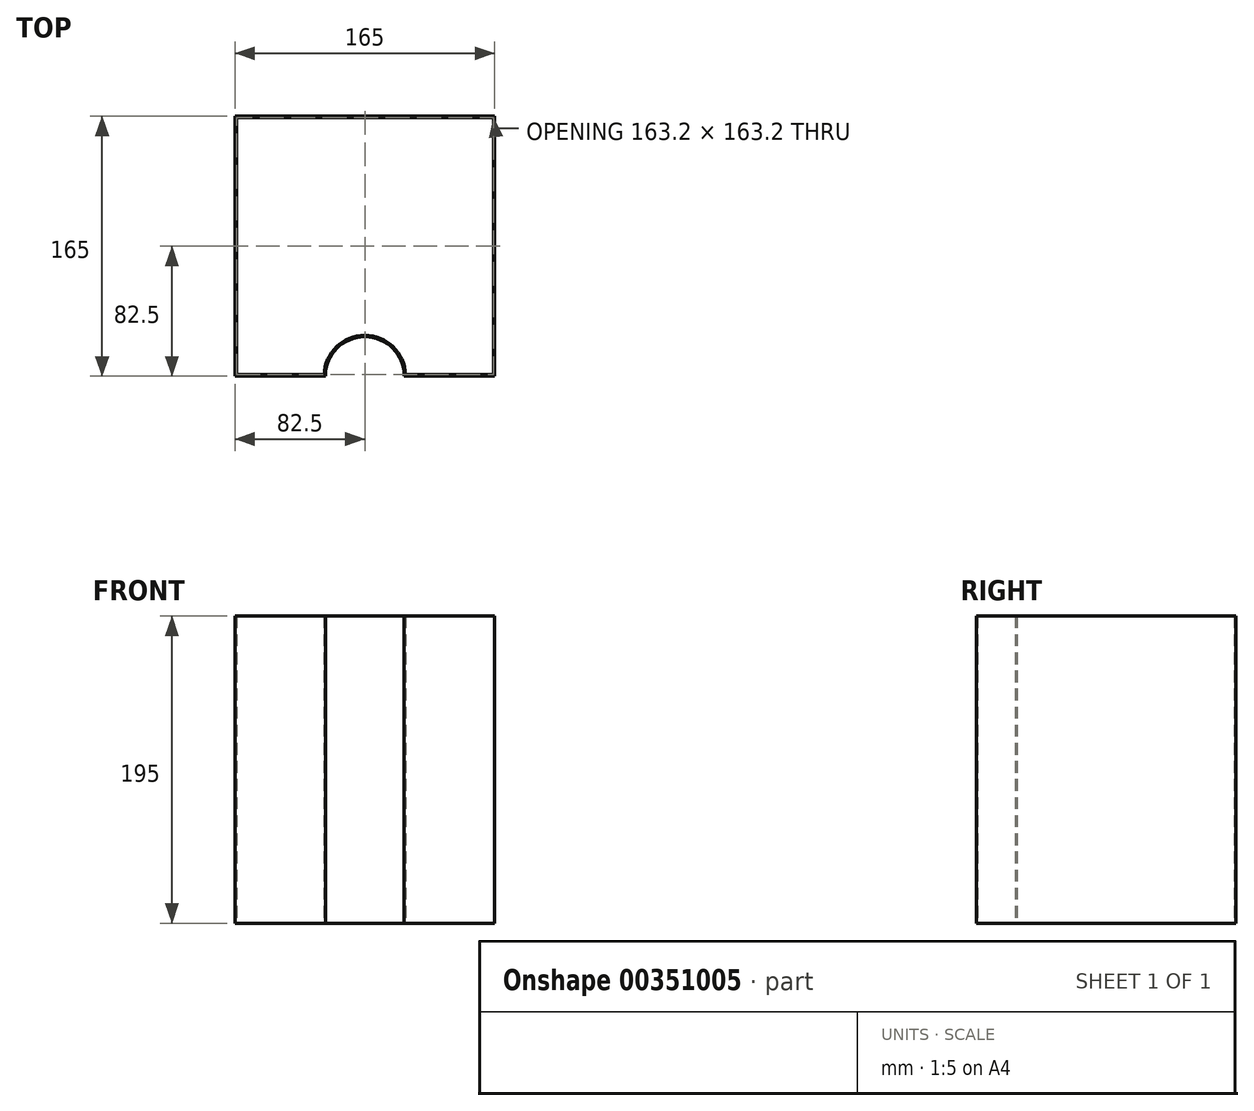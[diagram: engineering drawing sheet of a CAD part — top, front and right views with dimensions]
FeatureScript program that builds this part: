
annotation { "Feature Type Name" : "Feature", "Feature Type Description" : "" }
export const myFeature = defineFeature(function(context is Context, id is Id, definition is map)
    precondition{}
    {
        {
            var Q0;
            Q0=qCreatedBy(makeId("Top.planeOp"),FACE);
            var sketch = newSketch(context, id + "F0", { "sketchPlane" : qUnion([Q0])});
            skLineSegment(sketch, "E0.bottom", {"start": v(0, 0) * mm, "end": v(57.5, 0) * mm});
            skLineSegment(sketch, "E0.top", {"start": v(0, 165) * mm, "end": v(165, 165) * mm});
            skLineSegment(sketch, "E0.left", {"start": v(0, 0) * mm, "end": v(0, 165) * mm});
            skLineSegment(sketch, "E0.right", {"start": v(165, 0) * mm, "end": v(165, 165) * mm});
            skLineSegment(sketch, "E1.0", {"start": v(0.9, 0.9) * mm, "end": v(0.9, 164.1) * mm});
            skLineSegment(sketch, "E1.1", {"start": v(0.9, 0.9) * mm, "end": v(56.62, 0.9) * mm});
            skLineSegment(sketch, "E1.2", {"start": v(164.1, 0.9) * mm, "end": v(164.1, 164.1) * mm});
            skLineSegment(sketch, "E1.3", {"start": v(0.9, 164.1) * mm, "end": v(164.1, 164.1) * mm});
            skLineSegment(sketch, "E2", {"start": v(82.5, 165) * mm, "end": v(82.5, 0) * mm, "construction": true});
            skArc(sketch, "E3", {"start": v(107.5, 0) * mm, "mid": v(82.5, 25) * mm, "end": v(57.5, 0) * mm});
            skLineSegment(sketch, "E4.trimOffspring", {"start": v(107.5, 0) * mm, "end": v(165, 0) * mm});
            skArc(sketch, "E5.0", {"start": v(108.38, 0.9) * mm, "mid": v(82.5, 25.9) * mm, "end": v(56.62, 0.9) * mm});
            skLineSegment(sketch, "E6.trimOffspring", {"start": v(108.38, 0.9) * mm, "end": v(164.1, 0.9) * mm});
            skLineSegment(sketch, "E7", {"start": v(57.5, 0) * mm, "end": v(82.5, 0) * mm, "construction": true});
            skLineSegment(sketch, "E8", {"start": v(82.5, 0) * mm, "end": v(107.5, 0) * mm, "construction": true});
            skSolve(sketch);
        }
        {
            var Q0;
            Q0 = qSketchRegion(id + "F0", true);
            extrude(context, id + "F1", {"entities" : qUnion([Q0]), "depth" : 195 * mm});
        }
    });
